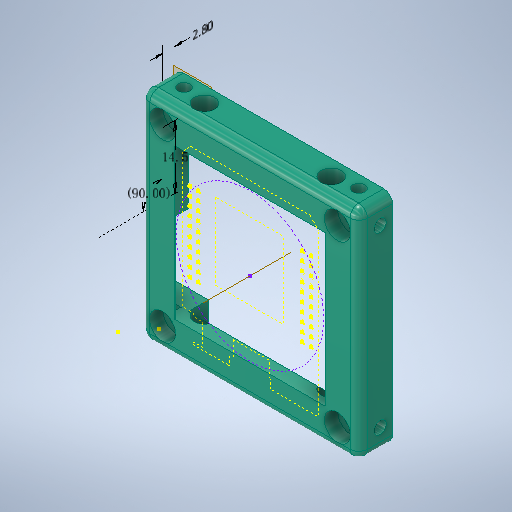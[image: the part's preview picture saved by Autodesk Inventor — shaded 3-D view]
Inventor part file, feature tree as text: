
AUTODESK INVENTOR PART (.ipt)
format: ipt  version: 2025.1 (Build 291241000, 241)  size: 623,104 bytes
history: native  units: mm
features: other x13, reference x13, sketch x11, hole x7, plane x3, extrude x3, fillet x1, chamfer x1, projected_geometry x1
ambient origin geometry x8: Origin, YZ Plane, XZ Plane, XY Plane, X Axis, Y Axis, Z Axis, Center Point
bodies: Solid1 (feature_tree)
feature tree (53):
  plane  "Work Plane1"
  extrude  "Extrusion1"  Depth=2.0mm
  fillet  "Fillet1"  Radius=49.8mm
  hole  "Hole1"  [1 undecoded]
  other  "Work Axis2"
  hole  "Hole2"  [1 undecoded]
  chamfer  "Chamfer2"  Distance=2.5mm
  hole  "Hole3"  [1 undecoded]
  hole  "Hole4"  [1 undecoded]
  hole  "Hole5"  [1 undecoded]
  extrude  "Extrusion3"  Depth=10.0mm
  sketch  "Sketch13"  dims[d39=2.5mm]
  plane  "Work Plane2"
  plane  "Work Plane3"
  hole  "Hole6"  [1 undecoded]
  extrude  "拉伸6"  Depth=10.0mm
  sketch  "草图16"  dims[d42=2.5mm]
  hole  "孔7"  [1 undecoded]
  sketch  "Sketch1"  dims[d0=7.7mm d1=0.0mm d2=2.0mm]
  reference  "Reference1"
  sketch  "Sketch2"  dims[d10=2.9mm d11=6.0mm d12=6.0mm d13=2.5mm d14=90.0deg d15=6.5mm d16=20.594885mm]
  other  "Work Axis1"
  sketch  "Sketch6"  dims[d20=3.2mm d21=6.0mm d22=6.0mm d23=3.1mm d24=90.0deg d25=12.0mm d26=20.594885mm]
  sketch  "Sketch7"  dims[d27=4.6mm d28=2.0mm d29=45.0deg d34=49.8mm]
  sketch  "Sketch8"  dims[d35=49.8mm d36=5.5mm]
  sketch  "Sketch9"  dims[d37=2.5mm d38=2.5mm]
  reference  "Reference5"
  reference  "Reference6"
  reference  "Reference7"
  reference  "Reference8"
  sketch  "Sketch14"  dims[d40=2.5mm]
  projected_geometry  "Projected Loop4"
  reference  "Reference9"
  reference  "Reference10"
  reference  "Reference11"
  reference  "Reference12"
  reference  "Reference13"
  reference  "Reference14"
  reference  "Reference15"
  reference  "Reference16"
  sketch  "草图15"  dims[d41=2.5mm]
  sketch  "草图17"  dims[d43=2.5mm d44=2.5mm d45=2.0mm d46=5.0mm d47=5.0mm d48=5.0mm d49=5.0mm d51=5.0mm d52=0.5mm d53=5.0mm d54=5.0mm d55=2.8mm d56=2.8mm d57=2.8mm d58=2.8mm d59=4.9mm d60=4.9mm d61=4.9mm d62=4.9mm d63=2.8mm d64=2.8mm d65=4.9mm d66=4.9mm d67=4.9mm d68=4.9mm d69=2.8mm d70=6.0mm d71=4.0mm d72=2.0mm d73=90.0deg d74=6.5mm d75=20.594885mm d76=2.8mm d77=6.0mm d78=4.0mm d79=2.0mm d80=90.0deg d81=6.5mm d82=20.594885mm d83=2.8mm d84=6.0mm d85=4.0mm d86=2.0mm d87=90.0deg d88=6.5mm d89=20.594885mm d90=7.7mm d91=135.0deg d92=135.0deg d93=10.0mm d94=0.0mm d105=0.7mm d106=6.0mm d107=4.0mm d108=2.0mm d109=90.0deg d110=8.0mm d111=20.594885mm d112=24.9mm d113=60.2mm d114=20.4mm d115=0.0mm d117=14.5mm d118=90.0deg d123=3.6mm d124=14.5mm d125=180.0deg d126=14.5mm d127=4.7mm d128=6.0mm d129=4.0mm d130=2.0mm d131=90.0deg d132=8.0mm d133=20.594885mm d116=2.8mm]
  other  "<userpath>\Dropbox\UC2\02_CAD\INVENTOR\uc2_v3\Assembly_Cube_empty_1x1_withBase_v3.iam"
  other  "Assembly_Cube_empty_1x1_withBase_v3.iam"
  other  "10_Cube_1x1_v3:1"
  other  "Assembly_Cube_empty_1x1_v2_IM.iam"
  other  "00_ESP32_Mini:1"
  other  "Assembly_Cube_empty_1x1_v2.iam"
  other  "10_Base_v2_puzzle:2"
  other  "线性尺寸 1"
  other  "10_Cube_1x1_v2_IM:1"
  other  "Assembly_Cube_v2.iam"
  other  "10_Cube_Base:1"
note: 7 required parameter values undecoded (feature->parameter linkage not recoverable at this tier; creation-order binding heuristic only, values carry confidence <= 0.55)
